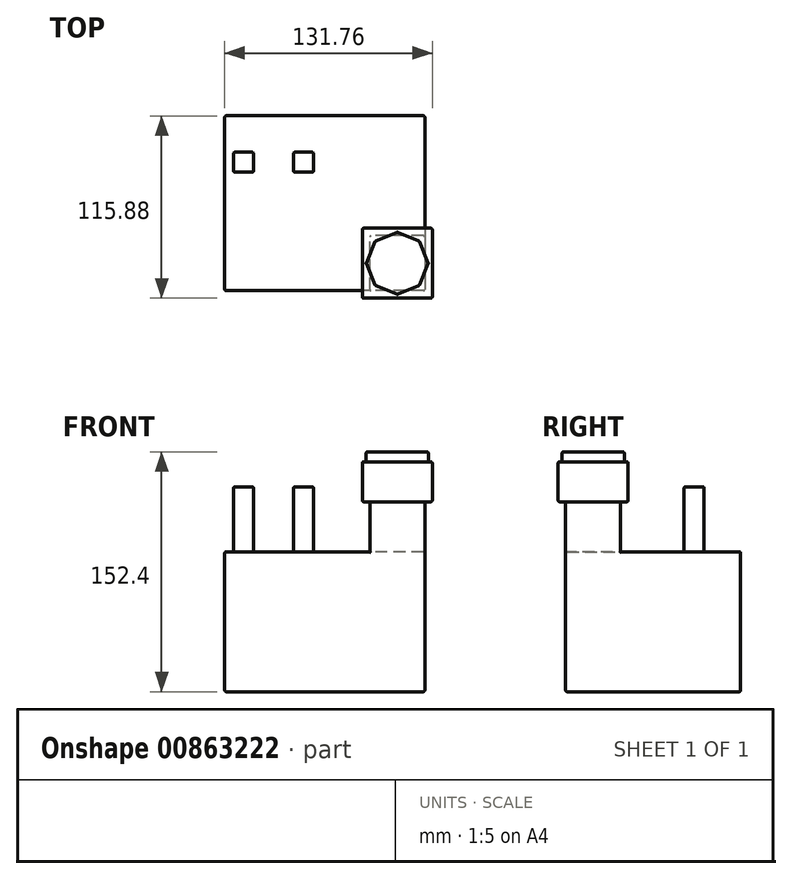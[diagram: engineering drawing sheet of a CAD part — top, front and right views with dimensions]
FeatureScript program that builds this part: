
annotation { "Feature Type Name" : "Feature", "Feature Type Description" : "" }
export const myFeature = defineFeature(function(context is Context, id is Id, definition is map)
    precondition{}
    {
        {
            var Q0;
            Q0=qCreatedBy(makeId("Top.planeOp"),FACE);
            var sketch = newSketch(context, id + "F0", { "sketchPlane" : qUnion([Q0])});
            skLineSegment(sketch, "E0.bottom", {"start": v(63.5, 55.56) * mm, "end": v(-63.5, 55.56) * mm});
            skLineSegment(sketch, "E0.top", {"start": v(63.5, -55.56) * mm, "end": v(-63.5, -55.56) * mm});
            skLineSegment(sketch, "E0.left", {"start": v(63.5, 55.56) * mm, "end": v(63.5, -55.56) * mm});
            skLineSegment(sketch, "E0.right", {"start": v(-63.5, 55.56) * mm, "end": v(-63.5, -55.56) * mm});
            skPoint(sketch, "E0.middle", {"position": v(0, 0) * mm});
            skSolve(sketch);
        }
        {
            var Q0;
            Q0=makeQuery(id+"F0.imprint","IMPRINT",FACE,{"disambiguationData":[TD([[makeQuery(id+"F0.imprint","IMPRINT",EDGE,{"derivedFrom":sQuery(id+"F0.wireOp",EDGE,"E0.bottom")}),1.0]])]});
            extrude(context, id + "F1", {"entities" : qUnion([Q0]), "depth" : 88.9 * mm, "offsetDistance" : 25.4 * mm});
        }
        {
            var Q0;
            Q0=makeQuery(id+"F1.opExtrude","CAP_FACE",FACE,{"disambiguationData":[OSD([sQuery(id+"F0.wireOp",EDGE,"E0.bottom"),sQuery(id+"F0.wireOp",EDGE,"E0.top"),sQuery(id+"F0.wireOp",EDGE,"E0.left"),sQuery(id+"F0.wireOp",EDGE,"E0.right")])],"isStart":false});
            var sketch = newSketch(context, id + "F2", { "sketchPlane" : qUnion([Q0])});
            skLineSegment(sketch, "E1.bottom", {"start": v(63.5, -55.56) * mm, "end": v(28.58, -55.56) * mm});
            skLineSegment(sketch, "E1.top", {"start": v(63.5, -20.64) * mm, "end": v(28.58, -20.64) * mm});
            skLineSegment(sketch, "E1.left", {"start": v(63.5, -55.56) * mm, "end": v(63.5, -20.64) * mm});
            skLineSegment(sketch, "E1.right", {"start": v(28.58, -55.56) * mm, "end": v(28.58, -20.64) * mm});
            skSolve(sketch);
        }
        {
            var Q0;
            Q0=makeQuery(id+"F2.imprint","IMPRINT",FACE,{"disambiguationData":[TD([[makeQuery(id+"F2.imprint","IMPRINT",EDGE,{"derivedFrom":sQuery(id+"F2.wireOp",EDGE,"E1.bottom")}),-1.0]])]});
            extrude(context, id + "F3", {"entities" : qUnion([Q0]), "operationType" : NewBodyOperationType.ADD, "depth" : 31.75 * mm, "offsetDistance" : 25.4 * mm});
        }
        {
            var Q0;
            Q0=makeQuery(id+"F3.opExtrude","CAP_FACE",FACE,{"disambiguationData":[OSD([sQuery(id+"F2.wireOp",EDGE,"E1.bottom"),sQuery(id+"F2.wireOp",EDGE,"E1.top"),sQuery(id+"F2.wireOp",EDGE,"E1.left"),sQuery(id+"F2.wireOp",EDGE,"E1.right")])],"isStart":false});
            var sketch = newSketch(context, id + "F4", { "sketchPlane" : qUnion([Q0])});
            skLineSegment(sketch, "E2", {"start": v(28.58, -20.64) * mm, "end": v(63.5, -55.56) * mm, "construction": true});
            skLineSegment(sketch, "E3", {"start": v(63.5, -20.64) * mm, "end": v(28.58, -55.56) * mm, "construction": true});
            skLineSegment(sketch, "E4.bottom", {"start": v(68.26, -60.33) * mm, "end": v(23.81, -60.33) * mm});
            skLineSegment(sketch, "E4.top", {"start": v(68.26, -15.88) * mm, "end": v(23.81, -15.88) * mm});
            skLineSegment(sketch, "E4.left", {"start": v(68.26, -60.33) * mm, "end": v(68.26, -15.88) * mm});
            skLineSegment(sketch, "E4.right", {"start": v(23.81, -60.33) * mm, "end": v(23.81, -15.88) * mm});
            skPoint(sketch, "E4.middle", {"position": v(46.04, -38.1) * mm});
            skSolve(sketch);
        }
        {
            var Q0;
            Q0 = qSketchRegion(id + "F4", true);
            extrude(context, id + "F5", {"entities" : qUnion([Q0]), "operationType" : NewBodyOperationType.ADD, "depth" : 25.4 * mm, "offsetDistance" : 25.4 * mm});
        }
        {
            var Q0;
            Q0=makeQuery(id+"F5.opExtrude","CAP_FACE",FACE,{"disambiguationData":[OSD([sQuery(id+"F4.wireOp",EDGE,"E4.bottom"),sQuery(id+"F4.wireOp",EDGE,"E4.top"),sQuery(id+"F4.wireOp",EDGE,"E4.left"),sQuery(id+"F4.wireOp",EDGE,"E4.right")])],"isStart":false});
            var sketch = newSketch(context, id + "F6", { "sketchPlane" : qUnion([Q0])});
            skLineSegment(sketch, "E5", {"start": v(23.81, -15.88) * mm, "end": v(68.26, -60.33) * mm, "construction": true});
            skLineSegment(sketch, "E6", {"start": v(68.26, -15.88) * mm, "end": v(23.81, -60.33) * mm, "construction": true});
            skLineSegment(sketch, "E7.bottom", {"start": v(63.76, -55.83) * mm, "end": v(28.31, -55.83) * mm, "construction": true});
            skLineSegment(sketch, "E7.top", {"start": v(63.76, -20.37) * mm, "end": v(28.31, -20.37) * mm, "construction": true});
            skLineSegment(sketch, "E7.left", {"start": v(63.76, -55.83) * mm, "end": v(63.76, -20.37) * mm, "construction": true});
            skLineSegment(sketch, "E7.right", {"start": v(28.31, -55.83) * mm, "end": v(28.31, -20.37) * mm, "construction": true});
            skPoint(sketch, "E7.middle", {"position": v(46.04, -38.1) * mm});
            skCircle(sketch, "E8.cCircle", {"center": v(46.04, -38.1) * mm, "radius": 19.77 * mm, "construction": true});
            skPoint(sketch, "E8.cCircle.perimeterSnap0", {"position": v(63.76, -38.1) * mm});
            skLineSegment(sketch, "E8.0", {"start": v(65.8, -38.1) * mm, "end": v(60.02, -52.08) * mm});
            skPoint(sketch, "E8.0.startSnap0", {"position": v(63.76, -38.1) * mm});
            skLineSegment(sketch, "E8.1", {"start": v(60.02, -52.08) * mm, "end": v(46.04, -57.87) * mm});
            skLineSegment(sketch, "E8.2", {"start": v(46.04, -57.87) * mm, "end": v(32.06, -52.08) * mm});
            skLineSegment(sketch, "E8.3", {"start": v(32.06, -52.08) * mm, "end": v(26.27, -38.1) * mm});
            skLineSegment(sketch, "E8.4", {"start": v(26.27, -38.1) * mm, "end": v(32.06, -24.12) * mm});
            skLineSegment(sketch, "E8.5", {"start": v(32.06, -24.12) * mm, "end": v(46.04, -18.33) * mm});
            skLineSegment(sketch, "E8.6", {"start": v(46.04, -18.33) * mm, "end": v(60.02, -24.12) * mm});
            skLineSegment(sketch, "E8.7", {"start": v(60.02, -24.12) * mm, "end": v(65.8, -38.1) * mm});
            skSolve(sketch);
        }
        {
            var Q0;
            Q0 = qSketchRegion(id + "F6", true);
            extrude(context, id + "F7", {"entities" : qUnion([Q0]), "operationType" : NewBodyOperationType.ADD, "depth" : 6.35 * mm, "offsetDistance" : 25.4 * mm});
        }
        {
            var Q0;
            Q0=makeQuery(id+"F1.opExtrude","CAP_FACE",FACE,{"disambiguationData":[OSD([sQuery(id+"F0.wireOp",EDGE,"E0.bottom"),sQuery(id+"F0.wireOp",EDGE,"E0.top"),sQuery(id+"F0.wireOp",EDGE,"E0.left"),sQuery(id+"F0.wireOp",EDGE,"E0.right")])],"isStart":false});
            var sketch = newSketch(context, id + "F8", { "sketchPlane" : qUnion([Q0])});
            skLineSegment(sketch, "E9", {"start": v(-52.46, 55.56) * mm, "end": v(-52.46, 32.4) * mm, "construction": true});
            skLineSegment(sketch, "E10", {"start": v(-63.5, 15.23) * mm, "end": v(-57.94, 15.08) * mm, "construction": true});
            skLineSegment(sketch, "E11.bottom", {"start": v(-57.94, 32.4) * mm, "end": v(-45.24, 32.4) * mm});
            skLineSegment(sketch, "E11.top", {"start": v(-57.94, 19.7) * mm, "end": v(-45.24, 19.7) * mm});
            skLineSegment(sketch, "E11.left", {"start": v(-57.94, 32.4) * mm, "end": v(-57.94, 19.7) * mm});
            skLineSegment(sketch, "E11.right", {"start": v(-45.24, 32.4) * mm, "end": v(-45.24, 19.7) * mm});
            skLineSegment(sketch, "E12", {"start": v(-45.24, 26.04) * mm, "end": v(-19.85, 26.3) * mm, "construction": true});
            skLineSegment(sketch, "E13.bottom", {"start": v(-19.85, 32.4) * mm, "end": v(-7.15, 32.4) * mm});
            skLineSegment(sketch, "E13.top", {"start": v(-19.85, 19.7) * mm, "end": v(-7.15, 19.7) * mm});
            skLineSegment(sketch, "E13.left", {"start": v(-19.85, 32.4) * mm, "end": v(-19.85, 19.7) * mm});
            skLineSegment(sketch, "E13.right", {"start": v(-7.15, 32.4) * mm, "end": v(-7.15, 19.7) * mm});
            skSolve(sketch);
        }
        {
            var Q0;
            Q0 = qSketchRegion(id + "F8", true);
            extrude(context, id + "F9", {"entities" : qUnion([Q0]), "operationType" : NewBodyOperationType.ADD, "depth" : 41.27 * mm, "offsetDistance" : 25.4 * mm});
        }
        {
            var Q0;
            Q0=makeQuery(id+"F1.opExtrude","CAP_EDGE",EDGE,{"disambiguationData":[OSD([sQuery(id+"F0.wireOp",EDGE,"E0.top")])],"isStart":false});
            var Q1;
            Q1=makeQuery(id+"F1.opExtrude","CAP_EDGE",EDGE,{"disambiguationData":[OSD([sQuery(id+"F0.wireOp",EDGE,"E0.right")])],"isStart":false});
            var Q2;
            Q2=makeQuery(id+"F1.opExtrude","SWEPT_EDGE",EDGE,{"disambiguationData":[OSD([sQuery(id+"F0.wireOp",EDGE,"E0.top"),sQuery(id+"F0.wireOp",EDGE,"E0.right")])]});
            var Q3;
            Q3=makeQuery(id+"F3.opExtrude","SWEPT_EDGE",EDGE,{"disambiguationData":[OSD([sQuery(id+"F0.wireOp",EDGE,"E0.top"),sQuery(id+"F2.wireOp",EDGE,"E1.bottom"),sQuery(id+"F2.wireOp",EDGE,"E1.right")])]});
            var Q4;
            Q4=makeQuery(id+"F3.boolean.opBoolean","MERGE",EDGE,{"derivedFrom":[makeQuery(id+"F1.opExtrude","SWEPT_EDGE",EDGE,{"disambiguationData":[OSD([sQuery(id+"F0.wireOp",EDGE,"E0.top"),sQuery(id+"F0.wireOp",EDGE,"E0.left")])]}),makeQuery(id+"F3.opExtrude","SWEPT_EDGE",EDGE,{"disambiguationData":[OSD([sQuery(id+"F2.wireOp",EDGE,"E1.bottom"),sQuery(id+"F2.wireOp",EDGE,"E1.left")])]})]});
            var Q5;
            Q5=makeQuery(id+"F3.opExtrude","SWEPT_EDGE",EDGE,{"disambiguationData":[OSD([sQuery(id+"F2.wireOp",EDGE,"E1.top"),sQuery(id+"F2.wireOp",EDGE,"E1.right")])]});
            var Q6;
            Q6=makeQuery(id+"F5.opExtrude","SWEPT_EDGE",EDGE,{"disambiguationData":[OSD([sQuery(id+"F4.wireOp",EDGE,"E4.top"),sQuery(id+"F4.wireOp",EDGE,"E4.right")])]});
            var Q7;
            Q7=makeQuery(id+"F5.opExtrude","SWEPT_EDGE",EDGE,{"disambiguationData":[OSD([sQuery(id+"F4.wireOp",EDGE,"E4.bottom"),sQuery(id+"F4.wireOp",EDGE,"E4.right")])]});
            var Q8;
            Q8=makeQuery(id+"F5.opExtrude","SWEPT_EDGE",EDGE,{"disambiguationData":[OSD([sQuery(id+"F4.wireOp",EDGE,"E4.bottom"),sQuery(id+"F4.wireOp",EDGE,"E4.left")])]});
            var Q9;
            Q9=makeQuery(id+"F5.opExtrude","CAP_EDGE",EDGE,{"disambiguationData":[OSD([sQuery(id+"F4.wireOp",EDGE,"E4.bottom")])],"isStart":true});
            var Q10;
            Q10=makeQuery(id+"F5.opExtrude","CAP_EDGE",EDGE,{"disambiguationData":[OSD([sQuery(id+"F4.wireOp",EDGE,"E4.right")])],"isStart":true});
            var Q11;
            Q11=makeQuery(id+"F5.opExtrude","CAP_EDGE",EDGE,{"disambiguationData":[OSD([sQuery(id+"F4.wireOp",EDGE,"E4.bottom")])],"isStart":false});
            var Q12;
            Q12=makeQuery(id+"F5.opExtrude","CAP_EDGE",EDGE,{"disambiguationData":[OSD([sQuery(id+"F4.wireOp",EDGE,"E4.right")])],"isStart":false});
            var Q13;
            Q13=makeQuery(id+"F5.opExtrude","CAP_EDGE",EDGE,{"disambiguationData":[OSD([sQuery(id+"F4.wireOp",EDGE,"E4.left")])],"isStart":false});
            var Q14;
            Q14=makeQuery(id+"F5.opExtrude","CAP_EDGE",EDGE,{"disambiguationData":[OSD([sQuery(id+"F4.wireOp",EDGE,"E4.top")])],"isStart":false});
            var Q15;
            Q15=makeQuery(id+"F7.opExtrude","CAP_EDGE",EDGE,{"disambiguationData":[OSD([sQuery(id+"F6.wireOp",EDGE,"E8.6")])],"isStart":false});
            var Q16;
            Q16=makeQuery(id+"F7.opExtrude","CAP_EDGE",EDGE,{"disambiguationData":[OSD([sQuery(id+"F6.wireOp",EDGE,"E8.7")])],"isStart":false});
            var Q17;
            Q17=makeQuery(id+"F7.opExtrude","CAP_EDGE",EDGE,{"disambiguationData":[OSD([sQuery(id+"F6.wireOp",EDGE,"E8.0")])],"isStart":false});
            var Q18;
            Q18=makeQuery(id+"F7.opExtrude","CAP_EDGE",EDGE,{"disambiguationData":[OSD([sQuery(id+"F6.wireOp",EDGE,"E8.1")])],"isStart":false});
            var Q19;
            Q19=makeQuery(id+"F7.opExtrude","CAP_EDGE",EDGE,{"disambiguationData":[OSD([sQuery(id+"F6.wireOp",EDGE,"E8.2")])],"isStart":false});
            var Q20;
            Q20=makeQuery(id+"F7.opExtrude","CAP_EDGE",EDGE,{"disambiguationData":[OSD([sQuery(id+"F6.wireOp",EDGE,"E8.3")])],"isStart":false});
            var Q21;
            Q21=makeQuery(id+"F7.opExtrude","CAP_EDGE",EDGE,{"disambiguationData":[OSD([sQuery(id+"F6.wireOp",EDGE,"E8.4")])],"isStart":false});
            var Q22;
            Q22=makeQuery(id+"F7.opExtrude","CAP_EDGE",EDGE,{"disambiguationData":[OSD([sQuery(id+"F6.wireOp",EDGE,"E8.5")])],"isStart":false});
            var Q23;
            Q23=makeQuery(id+"F7.opExtrude","SWEPT_EDGE",EDGE,{"disambiguationData":[OSD([sQuery(id+"F6.wireOp",EDGE,"E8.2"),sQuery(id+"F6.wireOp",EDGE,"E8.3")])]});
            var Q24;
            Q24=makeQuery(id+"F7.opExtrude","SWEPT_EDGE",EDGE,{"disambiguationData":[OSD([sQuery(id+"F6.wireOp",EDGE,"E8.1"),sQuery(id+"F6.wireOp",EDGE,"E8.2")])]});
            var Q25;
            Q25=makeQuery(id+"F7.opExtrude","SWEPT_EDGE",EDGE,{"disambiguationData":[OSD([sQuery(id+"F6.wireOp",EDGE,"E8.3"),sQuery(id+"F6.wireOp",EDGE,"E8.4")])]});
            var Q26;
            Q26=makeQuery(id+"F7.opExtrude","SWEPT_EDGE",EDGE,{"disambiguationData":[OSD([sQuery(id+"F6.wireOp",EDGE,"E8.0"),sQuery(id+"F6.wireOp",EDGE,"E8.1")])]});
            var Q27;
            Q27=makeQuery(id+"F7.opExtrude","SWEPT_EDGE",EDGE,{"disambiguationData":[OSD([sQuery(id+"F6.wireOp",EDGE,"E8.0"),sQuery(id+"F6.wireOp",EDGE,"E8.7")])]});
            var Q28;
            Q28=makeQuery(id+"F7.opExtrude","SWEPT_EDGE",EDGE,{"disambiguationData":[OSD([sQuery(id+"F6.wireOp",EDGE,"E8.6"),sQuery(id+"F6.wireOp",EDGE,"E8.7")])]});
            var Q29;
            Q29=makeQuery(id+"F7.opExtrude","SWEPT_EDGE",EDGE,{"disambiguationData":[OSD([sQuery(id+"F6.wireOp",EDGE,"E8.5"),sQuery(id+"F6.wireOp",EDGE,"E8.6")])]});
            var Q30;
            Q30=makeQuery(id+"F7.opExtrude","SWEPT_EDGE",EDGE,{"disambiguationData":[OSD([sQuery(id+"F6.wireOp",EDGE,"E8.4"),sQuery(id+"F6.wireOp",EDGE,"E8.5")])]});
            var Q31;
            Q31=makeQuery(id+"F5.opExtrude","SWEPT_EDGE",EDGE,{"disambiguationData":[OSD([sQuery(id+"F4.wireOp",EDGE,"E4.top"),sQuery(id+"F4.wireOp",EDGE,"E4.left")])]});
            var Q32;
            Q32=makeQuery(id+"F3.opExtrude","SWEPT_EDGE",EDGE,{"disambiguationData":[OSD([sQuery(id+"F0.wireOp",EDGE,"E0.left"),sQuery(id+"F2.wireOp",EDGE,"E1.top"),sQuery(id+"F2.wireOp",EDGE,"E1.left")])]});
            var Q33;
            Q33=makeQuery(id+"F5.opExtrude","CAP_EDGE",EDGE,{"disambiguationData":[OSD([sQuery(id+"F4.wireOp",EDGE,"E4.left")])],"isStart":true});
            var Q34;
            Q34=makeQuery(id+"F5.opExtrude","CAP_EDGE",EDGE,{"disambiguationData":[OSD([sQuery(id+"F4.wireOp",EDGE,"E4.top")])],"isStart":true});
            var Q35;
            Q35=makeQuery(id+"F1.opExtrude","CAP_EDGE",EDGE,{"disambiguationData":[OSD([sQuery(id+"F0.wireOp",EDGE,"E0.left")])],"isStart":false});
            var Q36;
            Q36=makeQuery(id+"F1.opExtrude","CAP_EDGE",EDGE,{"disambiguationData":[OSD([sQuery(id+"F0.wireOp",EDGE,"E0.bottom")])],"isStart":false});
            var Q37;
            Q37=makeQuery(id+"F1.opExtrude","SWEPT_EDGE",EDGE,{"disambiguationData":[OSD([sQuery(id+"F0.wireOp",EDGE,"E0.bottom"),sQuery(id+"F0.wireOp",EDGE,"E0.left")])]});
            var Q38;
            Q38=makeQuery(id+"F9.opExtrude","SWEPT_EDGE",EDGE,{"disambiguationData":[OSD([sQuery(id+"F8.wireOp",EDGE,"E11.bottom"),sQuery(id+"F8.wireOp",EDGE,"E11.left")])]});
            var Q39;
            Q39=makeQuery(id+"F9.opExtrude","SWEPT_EDGE",EDGE,{"disambiguationData":[OSD([sQuery(id+"F8.wireOp",EDGE,"E11.bottom"),sQuery(id+"F8.wireOp",EDGE,"E11.right")])]});
            var Q40;
            Q40=makeQuery(id+"F9.opExtrude","SWEPT_EDGE",EDGE,{"disambiguationData":[OSD([sQuery(id+"F8.wireOp",EDGE,"E11.top"),sQuery(id+"F8.wireOp",EDGE,"E11.left")])]});
            var Q41;
            Q41=makeQuery(id+"F9.opExtrude","CAP_EDGE",EDGE,{"disambiguationData":[OSD([sQuery(id+"F8.wireOp",EDGE,"E11.left")])],"isStart":false});
            var Q42;
            Q42=makeQuery(id+"F9.opExtrude","CAP_EDGE",EDGE,{"disambiguationData":[OSD([sQuery(id+"F8.wireOp",EDGE,"E11.bottom")])],"isStart":false});
            var Q43;
            Q43=makeQuery(id+"F9.opExtrude","CAP_EDGE",EDGE,{"disambiguationData":[OSD([sQuery(id+"F8.wireOp",EDGE,"E11.right")])],"isStart":false});
            var Q44;
            Q44=makeQuery(id+"F9.opExtrude","CAP_EDGE",EDGE,{"disambiguationData":[OSD([sQuery(id+"F8.wireOp",EDGE,"E11.top")])],"isStart":false});
            var Q45;
            Q45=makeQuery(id+"F9.opExtrude","SWEPT_EDGE",EDGE,{"disambiguationData":[OSD([sQuery(id+"F8.wireOp",EDGE,"E13.bottom"),sQuery(id+"F8.wireOp",EDGE,"E13.left")])]});
            var Q46;
            Q46=makeQuery(id+"F9.opExtrude","SWEPT_EDGE",EDGE,{"disambiguationData":[OSD([sQuery(id+"F8.wireOp",EDGE,"E13.bottom"),sQuery(id+"F8.wireOp",EDGE,"E13.right")])]});
            var Q47;
            Q47=makeQuery(id+"F9.opExtrude","CAP_EDGE",EDGE,{"disambiguationData":[OSD([sQuery(id+"F8.wireOp",EDGE,"E13.left")])],"isStart":false});
            var Q48;
            Q48=makeQuery(id+"F9.opExtrude","CAP_EDGE",EDGE,{"disambiguationData":[OSD([sQuery(id+"F8.wireOp",EDGE,"E13.bottom")])],"isStart":false});
            var Q49;
            Q49=makeQuery(id+"F9.opExtrude","CAP_EDGE",EDGE,{"disambiguationData":[OSD([sQuery(id+"F8.wireOp",EDGE,"E13.right")])],"isStart":false});
            var Q50;
            Q50=makeQuery(id+"F9.opExtrude","CAP_EDGE",EDGE,{"disambiguationData":[OSD([sQuery(id+"F8.wireOp",EDGE,"E13.top")])],"isStart":false});
            var Q51;
            Q51=makeQuery(id+"F9.opExtrude","SWEPT_EDGE",EDGE,{"disambiguationData":[OSD([sQuery(id+"F8.wireOp",EDGE,"E13.top"),sQuery(id+"F8.wireOp",EDGE,"E13.left")])]});
            var Q52;
            Q52=makeQuery(id+"F9.opExtrude","SWEPT_EDGE",EDGE,{"disambiguationData":[OSD([sQuery(id+"F8.wireOp",EDGE,"E13.top"),sQuery(id+"F8.wireOp",EDGE,"E13.right")])]});
            var Q53;
            Q53=makeQuery(id+"F9.opExtrude","SWEPT_EDGE",EDGE,{"disambiguationData":[OSD([sQuery(id+"F8.wireOp",EDGE,"E11.top"),sQuery(id+"F8.wireOp",EDGE,"E11.right")])]});
            var Q54;
            Q54=makeQuery(id+"F1.opExtrude","SWEPT_EDGE",EDGE,{"disambiguationData":[OSD([sQuery(id+"F0.wireOp",EDGE,"E0.bottom"),sQuery(id+"F0.wireOp",EDGE,"E0.right")])]});
            var Q55;
            Q55=makeQuery(id+"F1.opExtrude","CAP_EDGE",EDGE,{"disambiguationData":[OSD([sQuery(id+"F0.wireOp",EDGE,"E0.left")])],"isStart":true});
            var Q56;
            Q56=makeQuery(id+"F1.opExtrude","CAP_EDGE",EDGE,{"disambiguationData":[OSD([sQuery(id+"F0.wireOp",EDGE,"E0.bottom")])],"isStart":true});
            var Q57;
            Q57=makeQuery(id+"F1.opExtrude","CAP_EDGE",EDGE,{"disambiguationData":[OSD([sQuery(id+"F0.wireOp",EDGE,"E0.top")])],"isStart":true});
            var Q58;
            Q58=makeQuery(id+"F1.opExtrude","CAP_EDGE",EDGE,{"disambiguationData":[OSD([sQuery(id+"F0.wireOp",EDGE,"E0.right")])],"isStart":true});
            fillet(context, id + "F10", {"entities" : qUnion([Q0, Q1, Q2, Q3, Q4, Q5, Q6, Q7, Q8, Q9, Q10, Q11, Q12, Q13, Q14, Q15, Q16, Q17, Q18, Q19, Q20, Q21, Q22, Q23, Q24, Q25, Q26, Q27, Q28, Q29, Q30, Q31, Q32, Q33, Q34, Q35, Q36, Q37, Q38, Q39, Q40, Q41, Q42, Q43, Q44, Q45, Q46, Q47, Q48, Q49, Q50, Q51, Q52, Q53, Q54, Q55, Q56, Q57, Q58]), "radius" : 0.83 * mm, "tangentPropagation" : true, "allowEdgeOverflow" : false});
        }
    });
